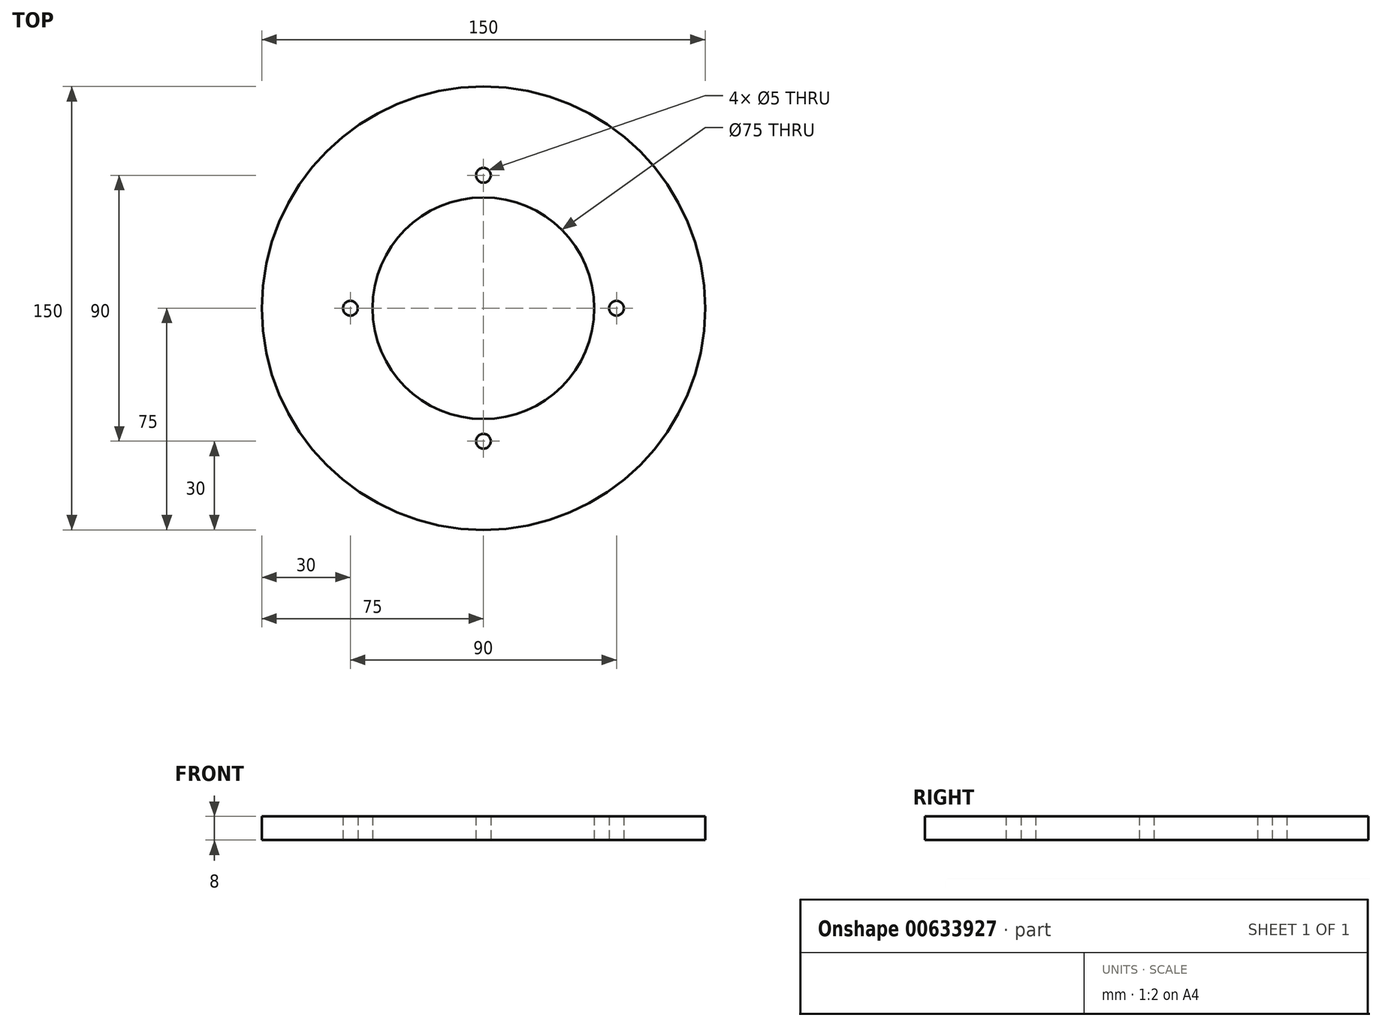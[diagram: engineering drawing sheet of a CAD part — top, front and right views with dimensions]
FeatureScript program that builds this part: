
annotation { "Feature Type Name" : "Feature", "Feature Type Description" : "" }
export const myFeature = defineFeature(function(context is Context, id is Id, definition is map)
    precondition{}
    {
        {
            var Q0;
            Q0=qCreatedBy(makeId("Top.planeOp"),FACE);
            var sketch = newSketch(context, id + "F0", { "sketchPlane" : qUnion([Q0])});
            skCircle(sketch, "E0", {"center": v(0, 0) * mm, "radius": 37.5 * mm});
            skCircle(sketch, "E1", {"center": v(0, 45) * mm, "radius": 2.5 * mm});
            skCircle(sketch, "E2.1.0", {"center": v(-45, 0) * mm, "radius": 2.5 * mm});
            skCircle(sketch, "E2.2.0", {"center": v(0, -45) * mm, "radius": 2.5 * mm});
            skCircle(sketch, "E2.3.0", {"center": v(45, 0) * mm, "radius": 2.5 * mm});
            skCircle(sketch, "E3", {"center": v(0, 0) * mm, "radius": 75 * mm});
            skSolve(sketch);
        }
        {
            var Q0;
            Q0=makeQuery(id+"F0.imprint","IMPRINT",FACE,{"disambiguationData":[TD([[makeQuery(id+"F0.imprint","IMPRINT",EDGE,{"derivedFrom":sQuery(id+"F0.wireOp",EDGE,"E0")}),-1.0]])]});
            extrude(context, id + "F1", {"entities" : qUnion([Q0]), "depth" : 8 * mm, "offsetDistance" : 25 * mm});
        }
    });
